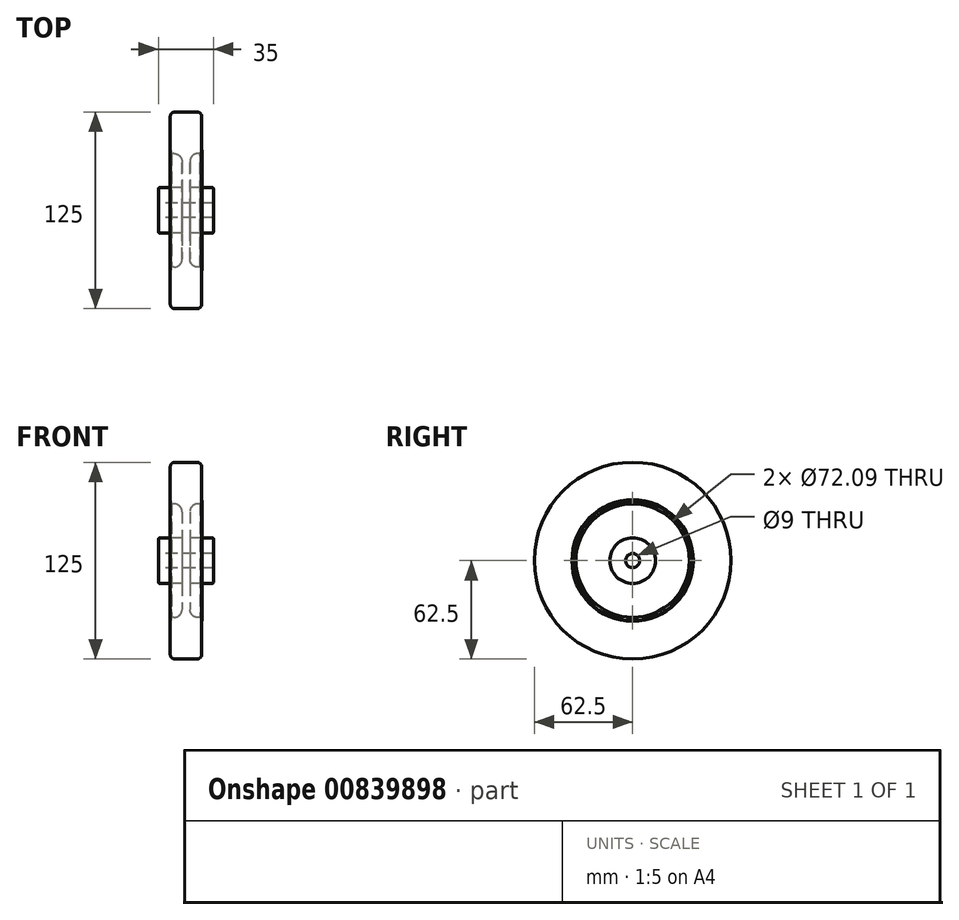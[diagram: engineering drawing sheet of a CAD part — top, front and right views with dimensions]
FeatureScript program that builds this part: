
annotation { "Feature Type Name" : "Feature", "Feature Type Description" : "" }
export const myFeature = defineFeature(function(context is Context, id is Id, definition is map)
    precondition{}
    {
        {
            var Q0;
            Q0=qCreatedBy(makeId("Top.planeOp"),FACE);
            var sketch = newSketch(context, id + "F0", { "sketchPlane" : qUnion([Q0])});
            skLineSegment(sketch, "E0", {"start": v(-40.1, 0) * mm, "end": v(41.82, 0) * mm, "construction": true});
            skLineSegment(sketch, "E1", {"start": v(0.86, 0) * mm, "end": v(0.86, 62.5) * mm, "construction": true});
            skLineSegment(sketch, "E2", {"start": v(0.86, 62.5) * mm, "end": v(-6.14, 62.5) * mm});
            skLineSegment(sketch, "E3", {"start": v(-1.64, 31.04) * mm, "end": v(-1.64, 14.5) * mm});
            skLineSegment(sketch, "E4", {"start": v(-1.64, 14.5) * mm, "end": v(-15.64, 14.5) * mm});
            skLineSegment(sketch, "E5", {"start": v(-16.64, 13.5) * mm, "end": v(-16.64, 4.5) * mm});
            skLineSegment(sketch, "E6", {"start": v(-16.64, 4.5) * mm, "end": v(0.86, 4.5) * mm});
            skLineSegment(sketch, "E7", {"start": v(-8.14, 37.5) * mm, "end": v(0.86, 37.5) * mm});
            skPoint(sketch, "E8.visualSharp", {"position": v(-3.83, 39.13) * mm});
            skPoint(sketch, "E9.visualSharp", {"position": v(-1.64, 37.5) * mm});
            skLineSegment(sketch, "E10", {"start": v(-8.14, 37.5) * mm, "end": v(-8.66, 38.05) * mm});
            skLineSegment(sketch, "E11", {"start": v(-8.66, 38.05) * mm, "end": v(-9.27, 38.05) * mm});
            skLineSegment(sketch, "E12", {"start": v(-6.64, 36.04) * mm, "end": v(-8.14, 36.04) * mm});
            skLineSegment(sketch, "E13", {"start": v(-8.14, 36.04) * mm, "end": v(-9.36, 37.9) * mm});
            skPoint(sketch, "E14.visualSharp", {"position": v(-9.46, 38.05) * mm});
            skArc(sketch, "E14.filletArc", {"start": v(-9.27, 38.05) * mm, "mid": v(-9.36, 38) * mm, "end": v(-9.36, 37.9) * mm});
            skPoint(sketch, "E15.visualSharp", {"position": v(-1.64, 36.04) * mm});
            skArc(sketch, "E15.filletArc", {"start": v(-1.64, 31.04) * mm, "mid": v(-3.1, 34.58) * mm, "end": v(-6.64, 36.04) * mm});
            skLineSegment(sketch, "E16", {"start": v(-9.14, 59.5) * mm, "end": v(-9.14, 38.57) * mm});
            skLineSegment(sketch, "E17", {"start": v(-9.14, 38.57) * mm, "end": v(-8.14, 37.5) * mm});
            skPoint(sketch, "E18.visualSharp", {"position": v(-9.14, 62.5) * mm});
            skArc(sketch, "E18.filletArc", {"start": v(-6.14, 62.5) * mm, "mid": v(-8.26, 61.62) * mm, "end": v(-9.14, 59.5) * mm});
            skLineSegment(sketch, "E19.MirrorCS", {"start": v(0.86, 62.5) * mm, "end": v(7.86, 62.5) * mm});
            skArc(sketch, "E20.MirrorCS", {"start": v(7.86, 62.5) * mm, "mid": v(9.98, 61.62) * mm, "end": v(10.86, 59.5) * mm});
            skLineSegment(sketch, "E21.MirrorCS", {"start": v(10.86, 59.5) * mm, "end": v(10.86, 38.57) * mm});
            skLineSegment(sketch, "E22.MirrorCS", {"start": v(10.86, 38.57) * mm, "end": v(9.86, 37.5) * mm});
            skLineSegment(sketch, "E23.MirrorCS", {"start": v(9.86, 37.5) * mm, "end": v(0.86, 37.5) * mm});
            skLineSegment(sketch, "E24.MirrorCS", {"start": v(9.86, 37.5) * mm, "end": v(10.37, 38.05) * mm});
            skLineSegment(sketch, "E25.MirrorCS", {"start": v(10.37, 38.05) * mm, "end": v(10.99, 38.05) * mm});
            skArc(sketch, "E26.MirrorCS", {"start": v(10.99, 38.05) * mm, "mid": v(11.08, 38) * mm, "end": v(11.07, 37.9) * mm});
            skLineSegment(sketch, "E27.MirrorCS", {"start": v(9.86, 36.04) * mm, "end": v(11.07, 37.9) * mm});
            skLineSegment(sketch, "E28.MirrorCS", {"start": v(8.36, 36.04) * mm, "end": v(9.86, 36.04) * mm});
            skArc(sketch, "E29.MirrorCS", {"start": v(3.36, 31.04) * mm, "mid": v(4.82, 34.58) * mm, "end": v(8.36, 36.04) * mm});
            skLineSegment(sketch, "E30.MirrorCS", {"start": v(3.36, 31.04) * mm, "end": v(3.36, 14.5) * mm});
            skLineSegment(sketch, "E31.MirrorCS", {"start": v(3.36, 14.5) * mm, "end": v(17.36, 14.5) * mm});
            skLineSegment(sketch, "E32.MirrorCS", {"start": v(18.36, 13.5) * mm, "end": v(18.36, 4.5) * mm});
            skLineSegment(sketch, "E33.MirrorCS", {"start": v(18.36, 4.5) * mm, "end": v(0.86, 4.5) * mm});
            skPoint(sketch, "E34.visualSharp", {"position": v(-16.64, 14.5) * mm});
            skArc(sketch, "E34.filletArc", {"start": v(-15.64, 14.5) * mm, "mid": v(-16.35, 14.2) * mm, "end": v(-16.64, 13.5) * mm});
            skPoint(sketch, "E35.visualSharp", {"position": v(18.36, 14.5) * mm});
            skArc(sketch, "E35.filletArc", {"start": v(18.36, 13.5) * mm, "mid": v(18.07, 14.2) * mm, "end": v(17.36, 14.5) * mm});
            skSolve(sketch);
        }
        {
            var Q0;
            Q0=makeQuery(id+"F0.imprint","IMPRINT",FACE,{"disambiguationData":[TD([[makeQuery(id+"F0.imprint","IMPRINT",EDGE,{"derivedFrom":sQuery(id+"F0.wireOp",EDGE,"E3")}),1.0]])]});
            var Q1;
            Q1=makeQuery(id+"F0.imprint","IMPRINT",FACE,{"disambiguationData":[TD([[makeQuery(id+"F0.imprint","IMPRINT",EDGE,{"derivedFrom":sQuery(id+"F0.wireOp",EDGE,"E2")}),1.0]])]});
            var Q2;
            Q2=sQuery(id+"F0.wireOp",EDGE,"E0");
            revolve(context, id + "F1", {"surfaceOperationType" : NewSurfaceOperationType.NEW, "entities" : qUnion([Q0, Q1]), "axis" : qUnion([Q2]), "revolveType" : RevolveType.FULL});
        }
    });
